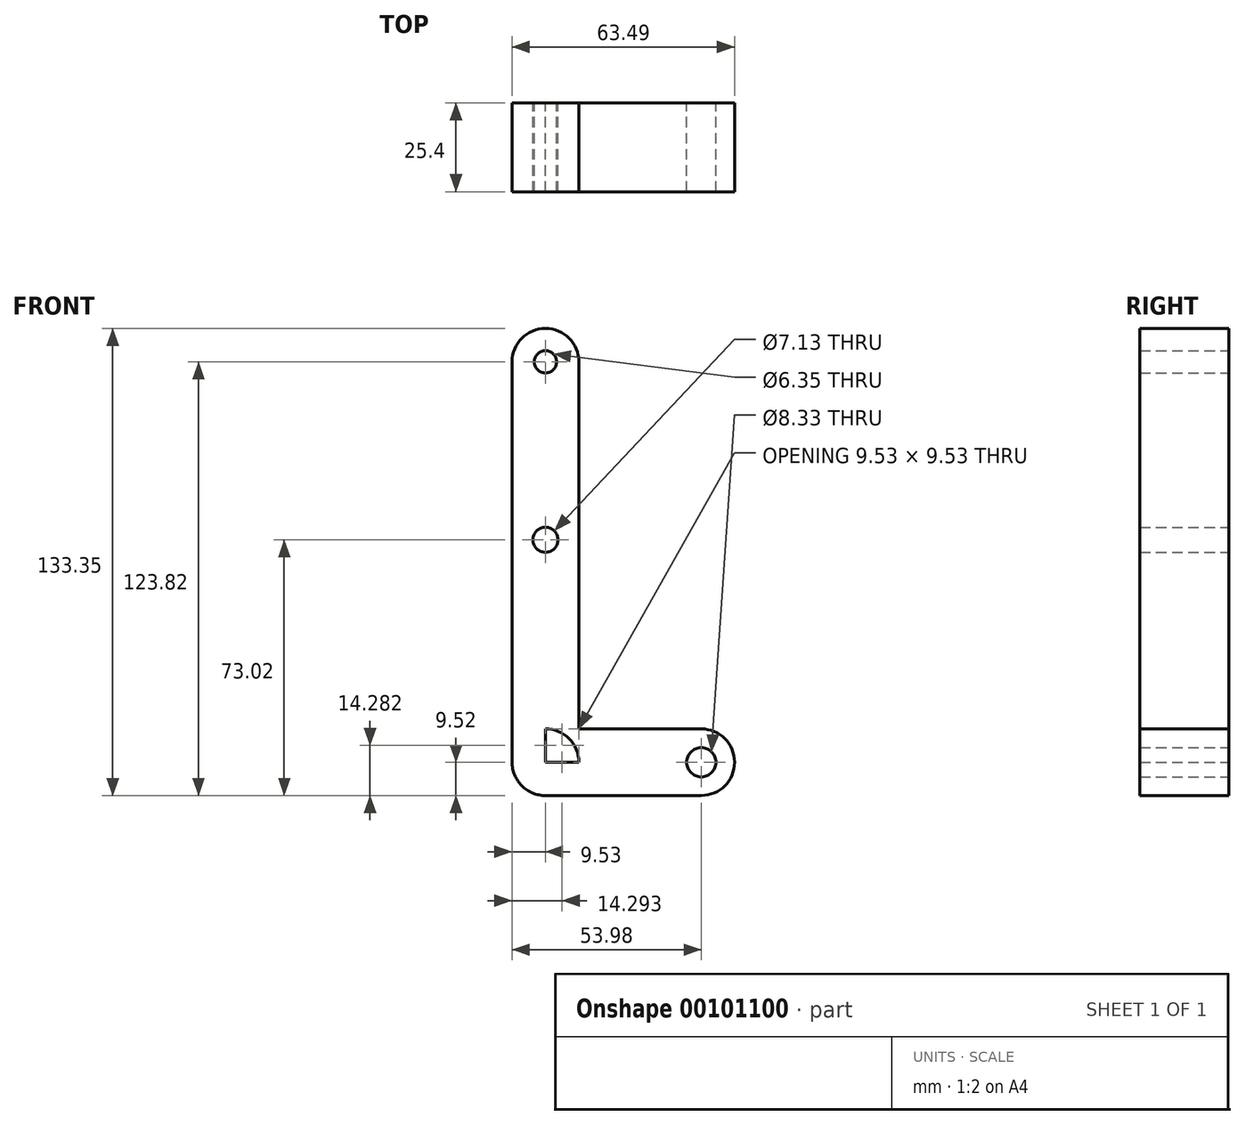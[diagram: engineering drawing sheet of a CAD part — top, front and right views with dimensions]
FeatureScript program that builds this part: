
annotation { "Feature Type Name" : "Feature", "Feature Type Description" : "" }
export const myFeature = defineFeature(function(context is Context, id is Id, definition is map)
    precondition{}
    {
        {
            var Q0;
            Q0=qCreatedBy(makeId("Front.planeOp"),FACE);
            var sketch = newSketch(context, id + "F0", { "sketchPlane" : qUnion([Q0])});
            skLineSegment(sketch, "E0", {"start": v(0, 114.3) * mm, "end": v(0, 0) * mm});
            skLineSegment(sketch, "E1", {"start": v(0, 0) * mm, "end": v(44.45, 0) * mm});
            skCircle(sketch, "E2", {"center": v(0, 114.3) * mm, "radius": 9.53 * mm});
            skCircle(sketch, "E3", {"center": v(0, 0) * mm, "radius": 9.53 * mm});
            skCircle(sketch, "E4", {"center": v(44.45, 0) * mm, "radius": 9.5 * mm});
            skLineSegment(sketch, "E5", {"start": v(0.57, 9.5) * mm, "end": v(44.45, 9.5) * mm});
            skLineSegment(sketch, "E6", {"start": v(0, -9.53) * mm, "end": v(44.48, -9.5) * mm});
            skLineSegment(sketch, "E7", {"start": v(-9.53, 63.5) * mm, "end": v(-9.53, 0) * mm});
            skLineSegment(sketch, "E8", {"start": v(-9.53, 114.3) * mm, "end": v(-9.53, 63.5) * mm});
            skLineSegment(sketch, "E9", {"start": v(9.53, 114.3) * mm, "end": v(9.53, 63.5) * mm});
            skLineSegment(sketch, "E10", {"start": v(9.53, 63.5) * mm, "end": v(9.53, 0) * mm});
            skCircle(sketch, "E11", {"center": v(-6.8, 104) * mm, "radius": 2.73 * mm});
            skCircle(sketch, "E12", {"center": v(0, 63.5) * mm, "radius": 3.57 * mm});
            skCircle(sketch, "E13", {"center": v(44.45, 0) * mm, "radius": 4.17 * mm});
            skCircle(sketch, "E14", {"center": v(0, 114.3) * mm, "radius": 3.18 * mm});
            skCircle(sketch, "E15", {"center": v(0, 63.5) * mm, "radius": 9.53 * mm});
            skSolve(sketch);
        }
        {
            var Q0;
            Q0 = qSketchRegion(id + "F0", true);
            extrude(context, id + "F1", {"entities" : qUnion([Q0]), "depth" : 25.4 * mm});
        }
    });
